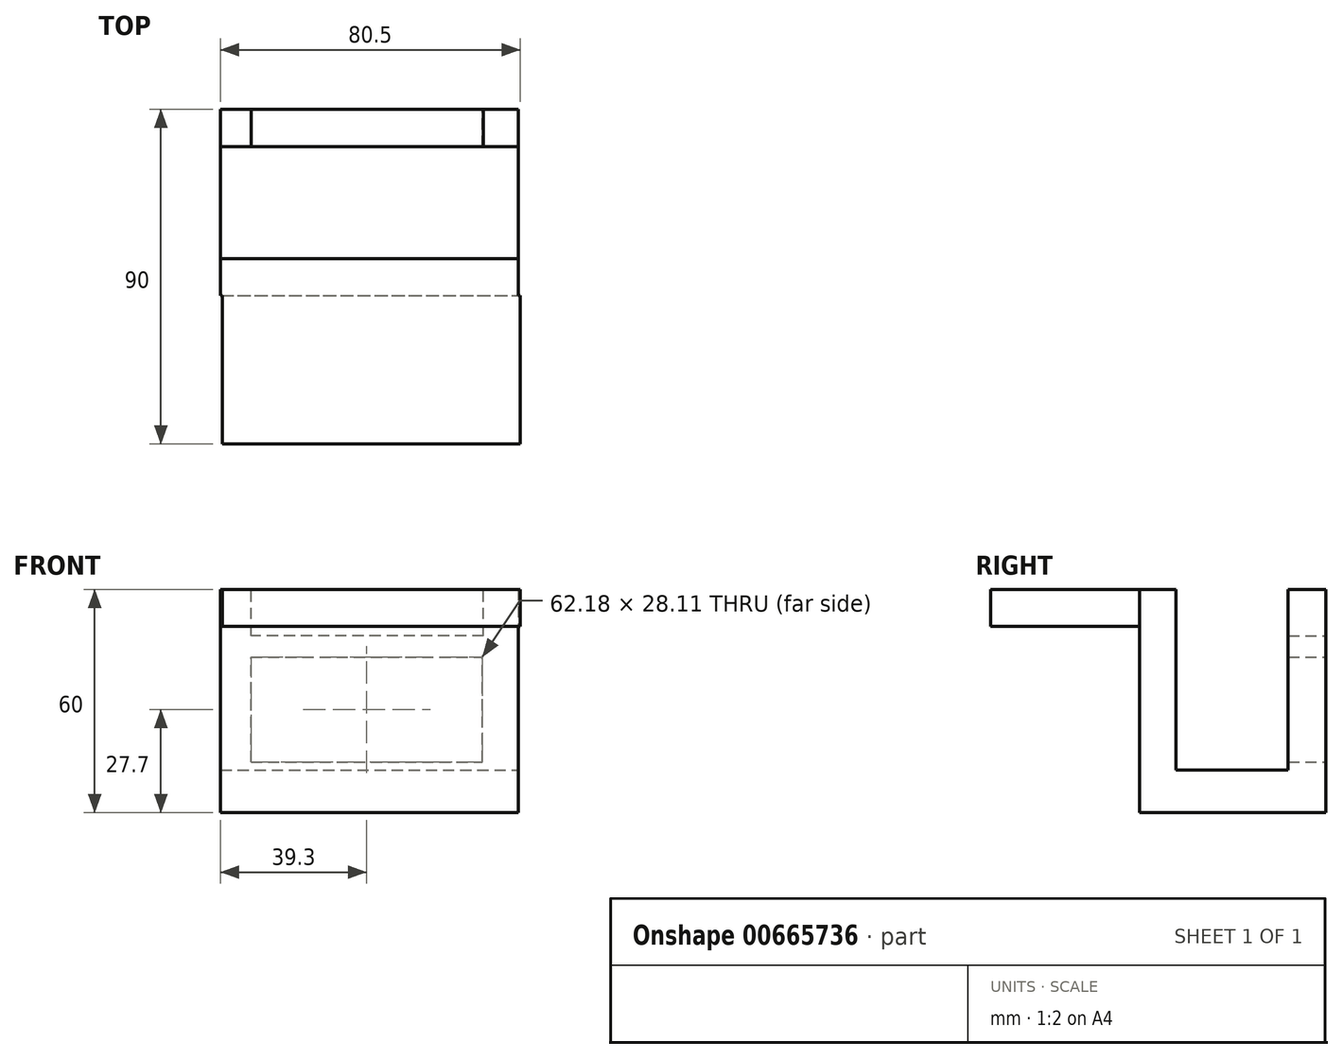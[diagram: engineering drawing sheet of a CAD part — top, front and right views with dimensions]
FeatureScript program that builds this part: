
annotation { "Feature Type Name" : "Feature", "Feature Type Description" : "" }
export const myFeature = defineFeature(function(context is Context, id is Id, definition is map)
    precondition{}
    {
        {
            var Q0;
            Q0=qCreatedBy(makeId("Top.planeOp"),FACE);
            var sketch = newSketch(context, id + "F0", { "sketchPlane" : qUnion([Q0])});
            skLineSegment(sketch, "E0.bottom", {"start": v(-39.67, 0) * mm, "end": v(40.33, 0) * mm});
            skLineSegment(sketch, "E0.top", {"start": v(-39.67, -40) * mm, "end": v(40.33, -40) * mm});
            skLineSegment(sketch, "E0.left", {"start": v(-39.67, 0) * mm, "end": v(-39.67, -40) * mm});
            skLineSegment(sketch, "E0.right", {"start": v(40.33, 0) * mm, "end": v(40.33, -40) * mm});
            skSolve(sketch);
        }
        {
            var Q0;
            Q0=qCreatedBy(makeId("Front.planeOp"),FACE);
            var sketch = newSketch(context, id + "F1", { "sketchPlane" : qUnion([Q0])});
            skLineSegment(sketch, "E1.bottom", {"start": v(-40.17, 0) * mm, "end": v(39.83, 0) * mm});
            skLineSegment(sketch, "E1.top", {"start": v(-40.17, -60) * mm, "end": v(39.83, -60) * mm});
            skLineSegment(sketch, "E1.left", {"start": v(-40.17, 0) * mm, "end": v(-40.17, -60) * mm});
            skLineSegment(sketch, "E1.right", {"start": v(39.83, 0) * mm, "end": v(39.83, -60) * mm});
            skSolve(sketch);
        }
        {
            var Q0;
            Q0=makeQuery(id+"F1.imprint","IMPRINT",FACE,{"disambiguationData":[TD([[makeQuery(id+"F1.imprint","IMPRINT",EDGE,{"derivedFrom":sQuery(id+"F1.wireOp",EDGE,"E1.bottom")}),-1.0]])]});
            extrude(context, id + "F2", {"entities" : qUnion([Q0]), "oppositeDirection" : true, "depth" : 50 * mm, "offsetDistance" : 25 * mm});
        }
        {
            var Q0;
            Q0=makeQuery(id+"F0.imprint","IMPRINT",FACE,{"disambiguationData":[TD([[makeQuery(id+"F0.imprint","IMPRINT",EDGE,{"derivedFrom":sQuery(id+"F0.wireOp",EDGE,"E0.bottom")}),-1.0]])]});
            extrude(context, id + "F3", {"entities" : qUnion([Q0]), "operationType" : NewBodyOperationType.ADD, "oppositeDirection" : true, "depth" : 10 * mm, "offsetDistance" : 25 * mm});
        }
        {
            var Q0;
            Q0=qCreatedBy(makeId("Right.planeOp"),FACE);
            var sketch = newSketch(context, id + "F4", { "sketchPlane" : qUnion([Q0])});
            skLineSegment(sketch, "E2.bottom", {"start": v(9.82, -48.63) * mm, "end": v(39.92, -48.63) * mm});
            skLineSegment(sketch, "E2.top", {"start": v(9.82, 29.47) * mm, "end": v(39.92, 29.47) * mm});
            skLineSegment(sketch, "E2.left", {"start": v(9.82, -48.63) * mm, "end": v(9.82, 29.47) * mm});
            skLineSegment(sketch, "E2.right", {"start": v(39.92, -48.63) * mm, "end": v(39.92, 29.47) * mm});
            skSolve(sketch);
        }
        {
            var Q0;
            Q0=makeQuery(id+"F4.imprint","IMPRINT",FACE,{"disambiguationData":[TD([[makeQuery(id+"F4.imprint","IMPRINT",EDGE,{"derivedFrom":sQuery(id+"F4.wireOp",EDGE,"E2.bottom")}),1.0]])]});
            extrude(context, id + "F5", {"entities" : qUnion([Q0]), "operationType" : NewBodyOperationType.REMOVE, "oppositeDirection" : true, "depth" : 50 * mm, "offsetDistance" : 25 * mm, "hasSecondDirection" : true, "secondDirectionOppositeDirection" : false, "secondDirectionDepth" : 50 * mm});
        }
        {
            var Q0;
            Q0=qCreatedBy(makeId("Front.planeOp"),FACE);
            cPlane(context, id + "F6", {"entities" : qUnion([Q0]), "cplaneType" : CPlaneType.OFFSET, "offset" : 50 * mm, "oppositeDirection" : true, "width" : 150 * mm, "height" : 150 * mm});
        }
        {
            var Q0;
            Q0=qCreatedBy(id+"F6.planeOp",FACE);
            var sketch = newSketch(context, id + "F7", { "sketchPlane" : qUnion([Q0])});
            skLineSegment(sketch, "E3.bottom", {"start": v(30.47, -12.56) * mm, "end": v(-31.96, -12.56) * mm});
            skLineSegment(sketch, "E3.top", {"start": v(30.47, 18.28) * mm, "end": v(-31.96, 18.28) * mm});
            skLineSegment(sketch, "E3.left", {"start": v(30.47, -12.56) * mm, "end": v(30.47, 18.28) * mm});
            skLineSegment(sketch, "E3.right", {"start": v(-31.96, -12.56) * mm, "end": v(-31.96, 18.28) * mm});
            skLineSegment(sketch, "E4.bottom", {"start": v(-31.96, -46.35) * mm, "end": v(30.22, -46.35) * mm});
            skLineSegment(sketch, "E4.top", {"start": v(-31.96, -18.25) * mm, "end": v(30.22, -18.25) * mm});
            skLineSegment(sketch, "E4.left", {"start": v(-31.96, -46.35) * mm, "end": v(-31.96, -18.25) * mm});
            skLineSegment(sketch, "E4.right", {"start": v(30.22, -46.35) * mm, "end": v(30.22, -18.25) * mm});
            skSolve(sketch);
        }
        {
            var Q0;
            Q0 = qSketchRegion(id + "F7", true);
            extrude(context, id + "F8", {"entities" : qUnion([Q0]), "operationType" : NewBodyOperationType.REMOVE, "depth" : 25 * mm, "offsetDistance" : 25 * mm});
        }
        {
            var Q0;
            Q0=qCreatedBy(makeId("Right.planeOp"),FACE);
            cPlane(context, id + "F9", {"entities" : qUnion([Q0]), "cplaneType" : CPlaneType.OFFSET, "offset" : 40 * mm, "width" : 150 * mm, "height" : 150 * mm});
        }
    });
